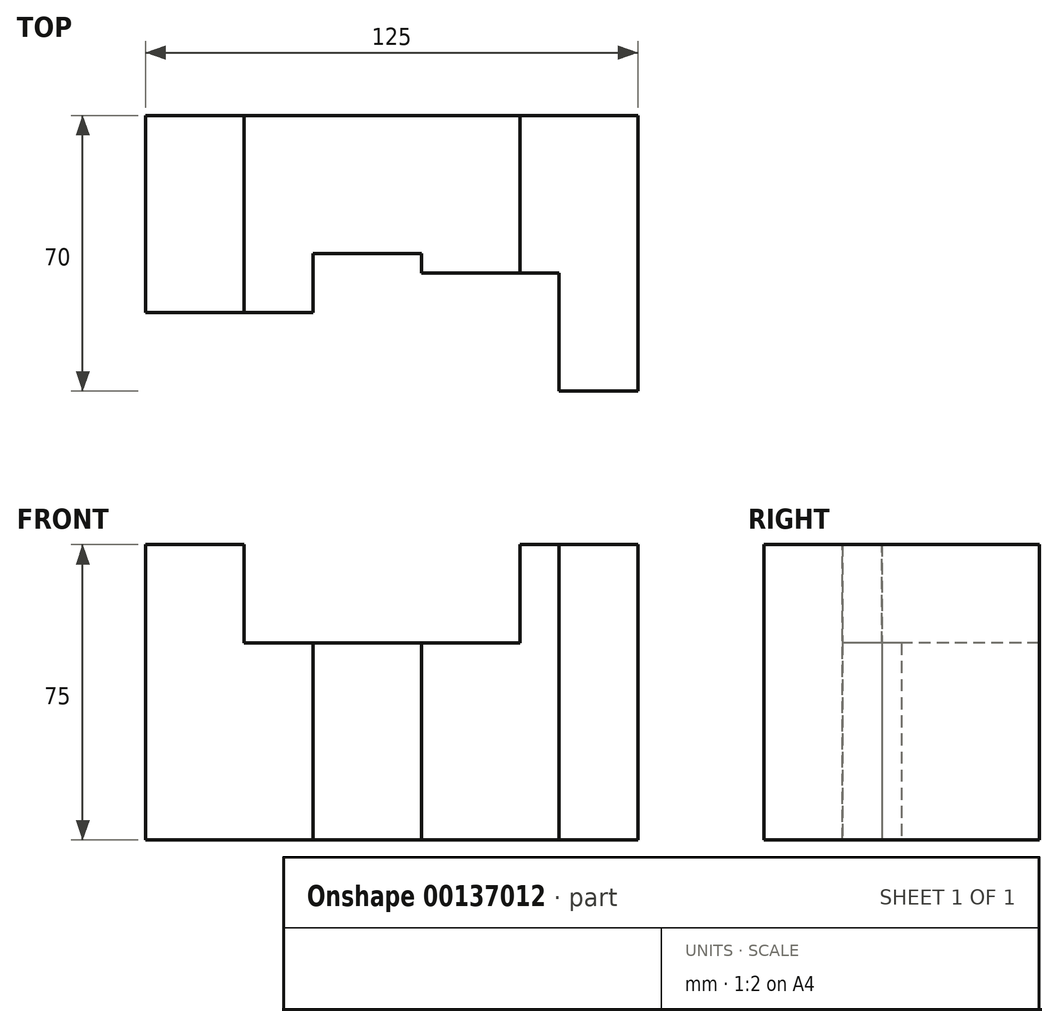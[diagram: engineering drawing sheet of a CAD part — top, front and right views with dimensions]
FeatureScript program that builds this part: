
annotation { "Feature Type Name" : "Feature", "Feature Type Description" : "" }
export const myFeature = defineFeature(function(context is Context, id is Id, definition is map)
    precondition{}
    {
        {
            var Q0;
            Q0=qCreatedBy(makeId("Front.planeOp"),FACE);
            var sketch = newSketch(context, id + "F0", { "sketchPlane" : qUnion([Q0])});
            skLineSegment(sketch, "E0", {"start": v(0, 0) * mm, "end": v(0, 0) * mm});
            skLineSegment(sketch, "E1", {"start": v(0, 0) * mm, "end": v(0, 75) * mm});
            skLineSegment(sketch, "E2", {"start": v(0, 75) * mm, "end": v(25, 75) * mm});
            skLineSegment(sketch, "E3", {"start": v(25, 75) * mm, "end": v(25, 50) * mm});
            skLineSegment(sketch, "E4", {"start": v(25, 50) * mm, "end": v(42.5, 50) * mm});
            skLineSegment(sketch, "E5", {"start": v(42.5, 50) * mm, "end": v(42.5, 0) * mm});
            skLineSegment(sketch, "E6", {"start": v(42.5, 50) * mm, "end": v(70, 50) * mm});
            skLineSegment(sketch, "E7", {"start": v(70, 50) * mm, "end": v(70, 0) * mm});
            skLineSegment(sketch, "E8", {"start": v(70, 0) * mm, "end": v(42.5, 0) * mm});
            skLineSegment(sketch, "E9", {"start": v(70, 50) * mm, "end": v(95, 50) * mm});
            skLineSegment(sketch, "E10", {"start": v(95, 50) * mm, "end": v(95, 75) * mm});
            skLineSegment(sketch, "E11", {"start": v(95, 75) * mm, "end": v(105, 75) * mm});
            skLineSegment(sketch, "E12", {"start": v(105, 75) * mm, "end": v(105, 0) * mm});
            skLineSegment(sketch, "E13", {"start": v(105, 0) * mm, "end": v(70, 0) * mm});
            skLineSegment(sketch, "E14", {"start": v(105, 75) * mm, "end": v(125, 75) * mm});
            skLineSegment(sketch, "E15", {"start": v(125, 75) * mm, "end": v(125, 0) * mm});
            skLineSegment(sketch, "E16", {"start": v(125, 0) * mm, "end": v(105, 0) * mm});
            skLineSegment(sketch, "E17", {"start": v(0, 0) * mm, "end": v(42.5, 0) * mm});
            skSolve(sketch);
        }
        {
            var Q0;
            Q0=makeQuery(id+"F0.imprint","IMPRINT",FACE,{"disambiguationData":[TD([[makeQuery(id+"F0.imprint","IMPRINT",EDGE,{"derivedFrom":sQuery(id+"F0.wireOp",EDGE,"E1")}),-1.0]])]});
            extrude(context, id + "F1", {"entities" : qUnion([Q0]), "oppositeDirection" : true, "depth" : 50 * mm});
        }
        {
            var Q0;
            Q0=makeQuery(id+"F0.imprint","IMPRINT",FACE,{"disambiguationData":[TD([[makeQuery(id+"F0.imprint","IMPRINT",EDGE,{"derivedFrom":sQuery(id+"F0.wireOp",EDGE,"E5")}),1.0]])]});
            var Q1;
            Q1=makeQuery(id+"F1.opExtrude","CAP_FACE",FACE,{"disambiguationData":[OSD([sQuery(id+"F0.wireOp",EDGE,"E1"),sQuery(id+"F0.wireOp",EDGE,"E2"),sQuery(id+"F0.wireOp",EDGE,"E3"),sQuery(id+"F0.wireOp",EDGE,"E4"),sQuery(id+"F0.wireOp",EDGE,"E5"),sQuery(id+"F0.wireOp",EDGE,"E17")])],"isStart":false});
            extrude(context, id + "F2", {"entities" : qUnion([Q0]), "operationType" : NewBodyOperationType.ADD, "endBound" : BoundingType.UP_TO_SURFACE, "oppositeDirection" : true, "endBoundEntityFace" : qUnion([Q1]), "depth" : 25 * mm, "hasSecondDirection" : true, "secondDirectionOppositeDirection" : true, "secondDirectionDepth" : 15 * mm});
        }
        {
            var Q0;
            Q0=makeQuery(id+"F0.imprint","IMPRINT",FACE,{"disambiguationData":[TD([[makeQuery(id+"F0.imprint","IMPRINT",EDGE,{"derivedFrom":sQuery(id+"F0.wireOp",EDGE,"E7")}),1.0]])]});
            var Q1;
            {var subQ0=sQuery(id+"F0.wireOp",EDGE,"E17");var subQ1=sQuery(id+"F0.wireOp",EDGE,"E5");var subQ2=sQuery(id+"F0.wireOp",EDGE,"E4");var subQ3=sQuery(id+"F0.wireOp",EDGE,"E3");var subQ4=sQuery(id+"F0.wireOp",EDGE,"E2");var subQ5=sQuery(id+"F0.wireOp",EDGE,"E1");Q1=makeQuery(id+"F2.boolean.opBoolean","MERGE",FACE,{"derivedFrom":[makeQuery(id+"F1.opExtrude","CAP_FACE",FACE,{"disambiguationData":[OSD([subQ5,subQ4,subQ3,subQ2,subQ1,subQ0])],"isStart":false}),makeQuery(id+"F2.opExtrude","CAP_FACE",FACE,{"disambiguationData":[OSD([subQ5,subQ4,subQ3,subQ2,subQ1,subQ0])],"isStart":false})]});}
            extrude(context, id + "F3", {"entities" : qUnion([Q0]), "operationType" : NewBodyOperationType.ADD, "endBound" : BoundingType.UP_TO_SURFACE, "oppositeDirection" : true, "endBoundEntityFace" : qUnion([Q1]), "depth" : 25 * mm, "hasSecondDirection" : true, "secondDirectionOppositeDirection" : true, "secondDirectionDepth" : 10 * mm});
        }
        {
            var Q0;
            Q0=makeQuery(id+"F0.imprint","IMPRINT",FACE,{"disambiguationData":[TD([[makeQuery(id+"F0.imprint","IMPRINT",EDGE,{"derivedFrom":sQuery(id+"F0.wireOp",EDGE,"E12")}),1.0]])]});
            var Q1;
            {var subQ0=sQuery(id+"F0.wireOp",EDGE,"E17");var subQ1=sQuery(id+"F0.wireOp",EDGE,"E5");var subQ2=sQuery(id+"F0.wireOp",EDGE,"E4");var subQ3=sQuery(id+"F0.wireOp",EDGE,"E3");var subQ4=sQuery(id+"F0.wireOp",EDGE,"E2");var subQ5=sQuery(id+"F0.wireOp",EDGE,"E1");Q1=makeQuery(id+"F3.boolean.opBoolean","MERGE",FACE,{"derivedFrom":[makeQuery(id+"F2.boolean.opBoolean","MERGE",FACE,{"derivedFrom":[makeQuery(id+"F1.opExtrude","CAP_FACE",FACE,{"disambiguationData":[OSD([subQ5,subQ4,subQ3,subQ2,subQ1,subQ0])],"isStart":false}),makeQuery(id+"F2.opExtrude","CAP_FACE",FACE,{"disambiguationData":[OSD([subQ5,subQ4,subQ3,subQ2,subQ1,subQ0])],"isStart":false})]}),makeQuery(id+"F3.opExtrude","CAP_FACE",FACE,{"disambiguationData":[OSD([subQ5,subQ4,subQ3,subQ2,subQ1,subQ0])],"isStart":false})]});}
            extrude(context, id + "F4", {"entities" : qUnion([Q0]), "operationType" : NewBodyOperationType.ADD, "endBound" : BoundingType.UP_TO_SURFACE, "oppositeDirection" : true, "endBoundEntityFace" : qUnion([Q1]), "depth" : 25 * mm, "hasSecondDirection" : true, "secondDirectionOppositeDirection" : false, "secondDirectionDepth" : 20 * mm});
        }
    });
